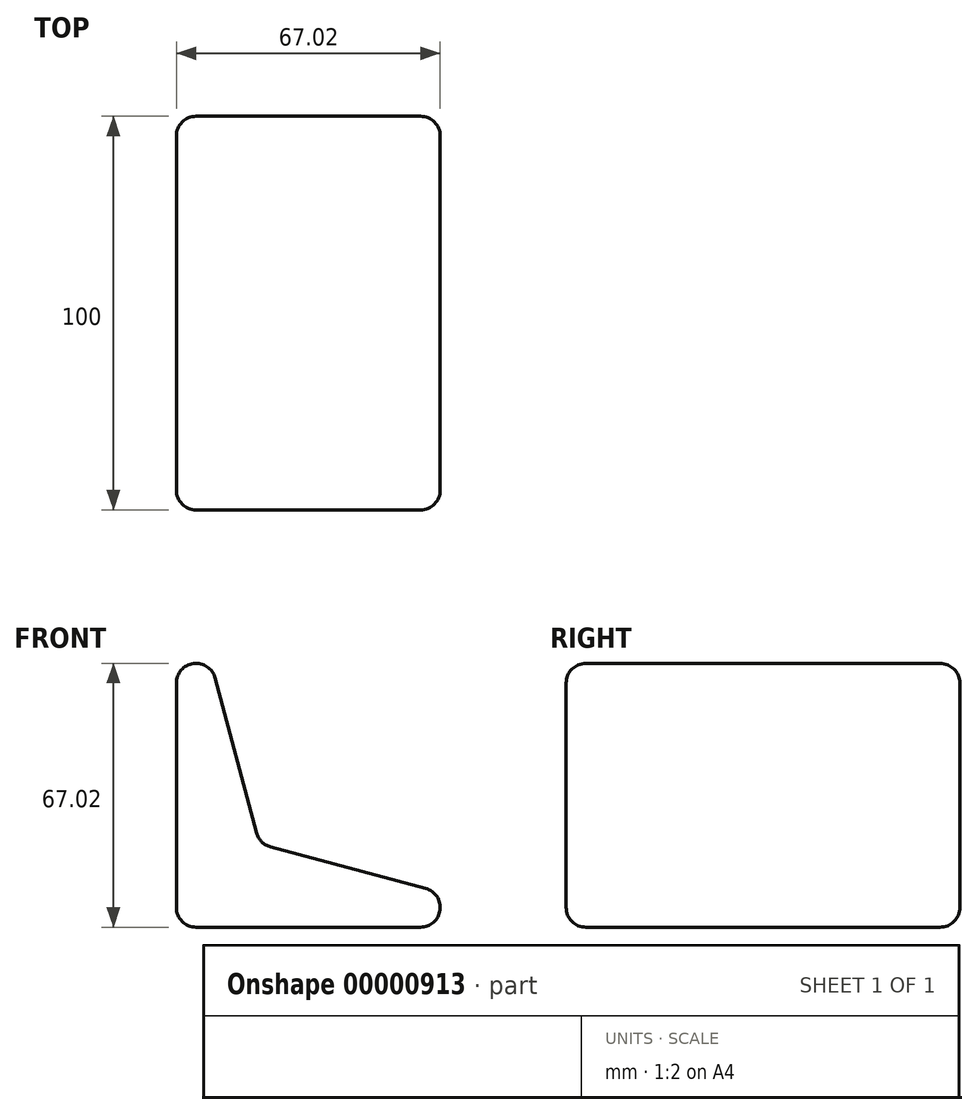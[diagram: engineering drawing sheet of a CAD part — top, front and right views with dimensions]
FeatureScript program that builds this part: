
annotation { "Feature Type Name" : "Feature", "Feature Type Description" : "" }
export const myFeature = defineFeature(function(context is Context, id is Id, definition is map)
    precondition{}
    {
        {
            var Q0;
            Q0=qCreatedBy(makeId("Front.planeOp"),FACE);
            var sketch = newSketch(context, id + "F0", { "sketchPlane" : qUnion([Q0])});
            skLineSegment(sketch, "E0.bottom", {"start": v(0, 0) * mm, "end": v(100, 0) * mm});
            skLineSegment(sketch, "E0.left", {"start": v(0, 0) * mm, "end": v(0, 100) * mm});
            skLineSegment(sketch, "E1", {"start": v(0, 100) * mm, "end": v(21.13, 21.13) * mm});
            skLineSegment(sketch, "E2", {"start": v(21.13, 21.13) * mm, "end": v(100, 0) * mm});
            skSolve(sketch);
        }
        {
            var Q0;
            Q0=makeQuery(id+"F0.imprint","IMPRINT",FACE,{"disambiguationData":[TD([[makeQuery(id+"F0.imprint","IMPRINT",EDGE,{"derivedFrom":sQuery(id+"F0.wireOp",EDGE,"E0.bottom")}),1.0]])]});
            extrude(context, id + "F1", {"entities" : qUnion([Q0]), "endBound" : BoundingType.SYMMETRIC, "depth" : 100 * mm});
        }
        {
            var Q0;
            Q0=makeQuery(id+"F1.opExtrude","SWEPT_EDGE",EDGE,{"disambiguationData":[OSD([sQuery(id+"F0.wireOp",EDGE,"E0.left"),sQuery(id+"F0.wireOp",EDGE,"E1")])]});
            var Q1;
            Q1=makeQuery(id+"F1.opExtrude","SWEPT_EDGE",EDGE,{"disambiguationData":[OSD([sQuery(id+"F0.wireOp",EDGE,"E1"),sQuery(id+"F0.wireOp",EDGE,"E2")])]});
            var Q2;
            Q2=makeQuery(id+"F1.opExtrude","SWEPT_EDGE",EDGE,{"disambiguationData":[OSD([sQuery(id+"F0.wireOp",EDGE,"E0.bottom"),sQuery(id+"F0.wireOp",EDGE,"E2")])]});
            var Q3;
            Q3=makeQuery(id+"F1.opExtrude","SWEPT_EDGE",EDGE,{"disambiguationData":[OSD([sQuery(id+"F0.wireOp",EDGE,"E0.bottom"),sQuery(id+"F0.wireOp",EDGE,"E0.left")])]});
            fillet(context, id + "F2", {"entities" : qUnion([Q0, Q1, Q2, Q3]), "radius" : 5 * mm, "tangentPropagation" : true, "allowEdgeOverflow" : false});
        }
        {
            var Q0;
            {var subQ0=sQuery(id+"F0.wireOp",EDGE,"E0.left");var subQ1=sQuery(id+"F0.wireOp",EDGE,"E1");Q0=makeQuery(id+"F2.opFillet","BLEND_EDGE",EDGE,{"blendedFrom":[makeQuery(id+"F1.opExtrude","SWEPT_EDGE",EDGE,{"disambiguationData":[OSD([subQ0,subQ1])]}),makeQuery(id+"F1.opExtrude","CAP_FACE",FACE,{"disambiguationData":[OSD([sQuery(id+"F0.wireOp",EDGE,"E0.bottom"),subQ0,subQ1,sQuery(id+"F0.wireOp",EDGE,"E2")])],"isStart":false})],"blendedInto":[makeQuery(id+"F1.opExtrude","CAP_FACE",FACE,{"disambiguationData":[OSD([sQuery(id+"F0.wireOp",EDGE,"E0.bottom"),subQ0,subQ1,sQuery(id+"F0.wireOp",EDGE,"E2")])],"isStart":false})]});}
            var Q1;
            {var subQ0=sQuery(id+"F0.wireOp",EDGE,"E0.left");var subQ1=sQuery(id+"F0.wireOp",EDGE,"E1");Q1=makeQuery(id+"F2.opFillet","BLEND_EDGE",EDGE,{"blendedFrom":[makeQuery(id+"F1.opExtrude","SWEPT_EDGE",EDGE,{"disambiguationData":[OSD([subQ0,subQ1])]}),makeQuery(id+"F1.opExtrude","CAP_FACE",FACE,{"disambiguationData":[OSD([sQuery(id+"F0.wireOp",EDGE,"E0.bottom"),subQ0,subQ1,sQuery(id+"F0.wireOp",EDGE,"E2")])],"isStart":true})],"blendedInto":[makeQuery(id+"F1.opExtrude","CAP_FACE",FACE,{"disambiguationData":[OSD([sQuery(id+"F0.wireOp",EDGE,"E0.bottom"),subQ0,subQ1,sQuery(id+"F0.wireOp",EDGE,"E2")])],"isStart":true})]});}
            fillet(context, id + "F3", {"entities" : qUnion([Q0, Q1]), "radius" : 5 * mm, "tangentPropagation" : true, "allowEdgeOverflow" : false});
        }
    });
